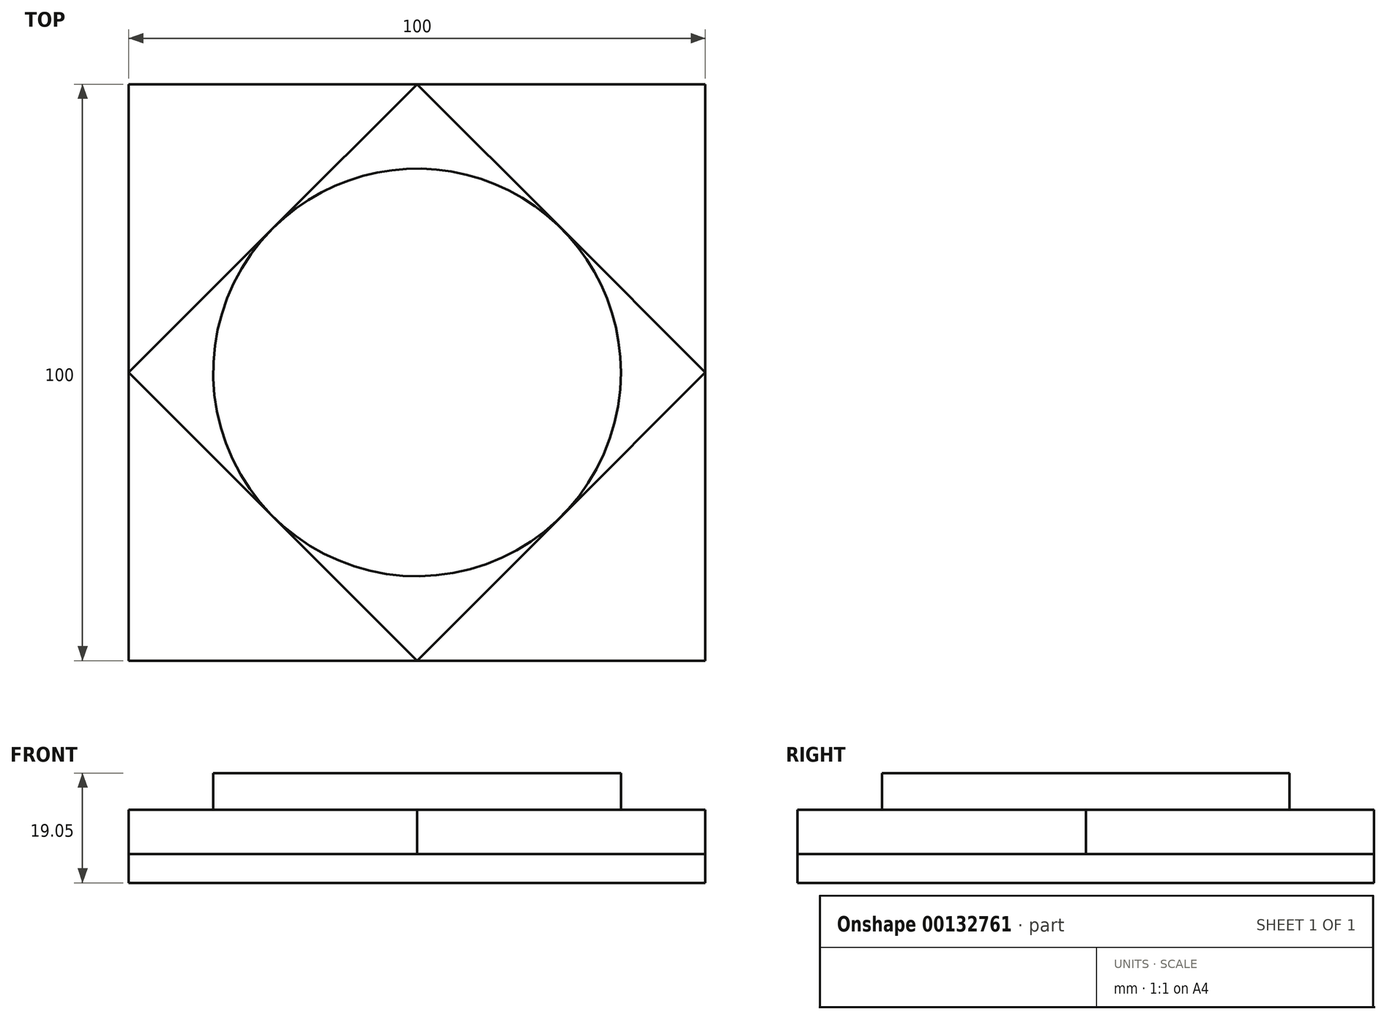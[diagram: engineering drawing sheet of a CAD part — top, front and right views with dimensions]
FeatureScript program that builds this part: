
annotation { "Feature Type Name" : "Feature", "Feature Type Description" : "" }
export const myFeature = defineFeature(function(context is Context, id is Id, definition is map)
    precondition{}
    {
        {
            var Q0;
            Q0=qCreatedBy(makeId("Top.planeOp"),FACE);
            var sketch = newSketch(context, id + "F0", { "sketchPlane" : qUnion([Q0])});
            skLineSegment(sketch, "E0.bottom", {"start": v(50, 50) * mm, "end": v(-50, 50) * mm});
            skLineSegment(sketch, "E0.top", {"start": v(50, -50) * mm, "end": v(-50, -50) * mm});
            skLineSegment(sketch, "E0.left", {"start": v(50, 50) * mm, "end": v(50, -50) * mm});
            skLineSegment(sketch, "E0.right", {"start": v(-50, 50) * mm, "end": v(-50, -50) * mm});
            skPoint(sketch, "E0.middle", {"position": v(0, 0) * mm});
            skCircle(sketch, "E1.cCircle", {"center": v(0, 0) * mm, "radius": 50 * mm, "construction": true});
            skLineSegment(sketch, "E1.0", {"start": v(50, 0) * mm, "end": v(0, -50) * mm});
            skLineSegment(sketch, "E1.1", {"start": v(0, -50) * mm, "end": v(-50, 0) * mm});
            skLineSegment(sketch, "E1.2", {"start": v(-50, 0) * mm, "end": v(0, 50) * mm});
            skLineSegment(sketch, "E1.3", {"start": v(0, 50) * mm, "end": v(50, 0) * mm});
            skCircle(sketch, "E2", {"center": v(0, 0) * mm, "radius": 35.36 * mm});
            skSolve(sketch);
        }
        {
            var Q0;
            {var subQ0=sQuery(id+"F0.wireOp",EDGE,"E0.left");var subQ1=sQuery(id+"F0.wireOp",EDGE,"E0.bottom");var subQ2=makeQuery(id+"F0.imprint","INTERSECT",VERTEX,{"derivedFrom":[subQ1,subQ0]});Q0=makeQuery(id+"F0.imprint","IMPRINT",FACE,{"disambiguationData":[TD([[makeQuery(id+"F0.imprint","IMPRINT",EDGE,{"disambiguationData":[TD([[subQ2,-1.0]])],"derivedFrom":subQ1}),1.0]])]});}
            var Q1;
            {var subQ0=sQuery(id+"F0.wireOp",EDGE,"E0.right");var subQ1=sQuery(id+"F0.wireOp",EDGE,"E0.bottom");var subQ2=makeQuery(id+"F0.imprint","INTERSECT",VERTEX,{"derivedFrom":[subQ1,subQ0]});Q1=makeQuery(id+"F0.imprint","IMPRINT",FACE,{"disambiguationData":[TD([[makeQuery(id+"F0.imprint","IMPRINT",EDGE,{"disambiguationData":[TD([[subQ2,1.0]])],"derivedFrom":subQ1}),1.0]])]});}
            var Q2;
            {var subQ0=sQuery(id+"F0.wireOp",EDGE,"E0.left");var subQ1=sQuery(id+"F0.wireOp",EDGE,"E0.top");var subQ2=makeQuery(id+"F0.imprint","INTERSECT",VERTEX,{"derivedFrom":[subQ1,subQ0]});Q2=makeQuery(id+"F0.imprint","IMPRINT",FACE,{"disambiguationData":[TD([[makeQuery(id+"F0.imprint","IMPRINT",EDGE,{"disambiguationData":[TD([[subQ2,-1.0]])],"derivedFrom":subQ1}),-1.0]])]});}
            var Q3;
            {var subQ0=sQuery(id+"F0.wireOp",EDGE,"E2");var subQ1=makeQuery(id+"F0.imprint","INTERSECT",VERTEX,{"derivedFrom":[sQuery(id+"F0.wireOp",EDGE,"E1.2"),subQ0]});Q3=makeQuery(id+"F0.imprint","IMPRINT",FACE,{"disambiguationData":[TD([[makeQuery(id+"F0.imprint","IMPRINT",EDGE,{"disambiguationData":[TD([[subQ1,1.0]])],"derivedFrom":subQ0}),1.0]])]});}
            var Q4;
            {var subQ1=sQuery(id+"F0.wireOp",EDGE,"E1.2");var subQ3=sQuery(id+"F0.wireOp",EDGE,"E2");var subQ4=makeQuery(id+"F0.imprint","INTERSECT",VERTEX,{"derivedFrom":[subQ1,subQ3]});Q4=makeQuery(id+"F0.imprint","IMPRINT",FACE,{"disambiguationData":[TD([[makeQuery(id+"F0.imprint","IMPRINT",EDGE,{"disambiguationData":[TD([[subQ4,1.0]])],"derivedFrom":subQ3}),-1.0]])]});}
            var Q5;
            {var subQ1=sQuery(id+"F0.wireOp",EDGE,"E1.1");var subQ3=sQuery(id+"F0.wireOp",EDGE,"E2");var subQ4=makeQuery(id+"F0.imprint","INTERSECT",VERTEX,{"derivedFrom":[subQ1,subQ3]});Q5=makeQuery(id+"F0.imprint","IMPRINT",FACE,{"disambiguationData":[TD([[makeQuery(id+"F0.imprint","IMPRINT",EDGE,{"disambiguationData":[TD([[subQ4,1.0]])],"derivedFrom":subQ3}),-1.0]])]});}
            var Q6;
            {var subQ0=sQuery(id+"F0.wireOp",EDGE,"E0.right");var subQ1=sQuery(id+"F0.wireOp",EDGE,"E0.top");var subQ2=makeQuery(id+"F0.imprint","INTERSECT",VERTEX,{"derivedFrom":[subQ1,subQ0]});Q6=makeQuery(id+"F0.imprint","IMPRINT",FACE,{"disambiguationData":[TD([[makeQuery(id+"F0.imprint","IMPRINT",EDGE,{"disambiguationData":[TD([[subQ2,1.0]])],"derivedFrom":subQ1}),-1.0]])]});}
            var Q7;
            {var subQ1=sQuery(id+"F0.wireOp",EDGE,"E1.0");var subQ3=sQuery(id+"F0.wireOp",EDGE,"E2");var subQ4=makeQuery(id+"F0.imprint","INTERSECT",VERTEX,{"derivedFrom":[subQ1,subQ3]});Q7=makeQuery(id+"F0.imprint","IMPRINT",FACE,{"disambiguationData":[TD([[makeQuery(id+"F0.imprint","IMPRINT",EDGE,{"disambiguationData":[TD([[subQ4,-1.0]])],"derivedFrom":subQ3}),-1.0]])]});}
            var Q8;
            {var subQ1=sQuery(id+"F0.wireOp",EDGE,"E1.0");var subQ3=sQuery(id+"F0.wireOp",EDGE,"E2");var subQ4=makeQuery(id+"F0.imprint","INTERSECT",VERTEX,{"derivedFrom":[subQ1,subQ3]});Q8=makeQuery(id+"F0.imprint","IMPRINT",FACE,{"disambiguationData":[TD([[makeQuery(id+"F0.imprint","IMPRINT",EDGE,{"disambiguationData":[TD([[subQ4,1.0]])],"derivedFrom":subQ3}),-1.0]])]});}
            extrude(context, id + "F1", {"entities" : qUnion([Q0, Q1, Q2, Q3, Q4, Q5, Q6, Q7, Q8]), "offsetDistance" : 25 * mm, "depth" : 5 * mm});
        }
        {
            var Q0;
            {var subQ1=sQuery(id+"F0.wireOp",EDGE,"E1.1");var subQ3=sQuery(id+"F0.wireOp",EDGE,"E2");var subQ4=makeQuery(id+"F0.imprint","INTERSECT",VERTEX,{"derivedFrom":[subQ1,subQ3]});Q0=makeQuery(id+"F0.imprint","IMPRINT",FACE,{"disambiguationData":[TD([[makeQuery(id+"F0.imprint","IMPRINT",EDGE,{"disambiguationData":[TD([[subQ4,1.0]])],"derivedFrom":subQ3}),-1.0]])]});}
            var Q1;
            {var subQ1=sQuery(id+"F0.wireOp",EDGE,"E1.0");var subQ3=sQuery(id+"F0.wireOp",EDGE,"E2");var subQ4=makeQuery(id+"F0.imprint","INTERSECT",VERTEX,{"derivedFrom":[subQ1,subQ3]});Q1=makeQuery(id+"F0.imprint","IMPRINT",FACE,{"disambiguationData":[TD([[makeQuery(id+"F0.imprint","IMPRINT",EDGE,{"disambiguationData":[TD([[subQ4,-1.0]])],"derivedFrom":subQ3}),-1.0]])]});}
            var Q2;
            {var subQ1=sQuery(id+"F0.wireOp",EDGE,"E1.0");var subQ3=sQuery(id+"F0.wireOp",EDGE,"E2");var subQ4=makeQuery(id+"F0.imprint","INTERSECT",VERTEX,{"derivedFrom":[subQ1,subQ3]});Q2=makeQuery(id+"F0.imprint","IMPRINT",FACE,{"disambiguationData":[TD([[makeQuery(id+"F0.imprint","IMPRINT",EDGE,{"disambiguationData":[TD([[subQ4,1.0]])],"derivedFrom":subQ3}),-1.0]])]});}
            var Q3;
            {var subQ0=sQuery(id+"F0.wireOp",EDGE,"E2");var subQ1=makeQuery(id+"F0.imprint","INTERSECT",VERTEX,{"derivedFrom":[sQuery(id+"F0.wireOp",EDGE,"E1.2"),subQ0]});Q3=makeQuery(id+"F0.imprint","IMPRINT",FACE,{"disambiguationData":[TD([[makeQuery(id+"F0.imprint","IMPRINT",EDGE,{"disambiguationData":[TD([[subQ1,1.0]])],"derivedFrom":subQ0}),1.0]])]});}
            var Q4;
            {var subQ1=sQuery(id+"F0.wireOp",EDGE,"E1.2");var subQ3=sQuery(id+"F0.wireOp",EDGE,"E2");var subQ4=makeQuery(id+"F0.imprint","INTERSECT",VERTEX,{"derivedFrom":[subQ1,subQ3]});Q4=makeQuery(id+"F0.imprint","IMPRINT",FACE,{"disambiguationData":[TD([[makeQuery(id+"F0.imprint","IMPRINT",EDGE,{"disambiguationData":[TD([[subQ4,1.0]])],"derivedFrom":subQ3}),-1.0]])]});}
            extrude(context, id + "F2", {"entities" : qUnion([Q0, Q1, Q2, Q3, Q4]), "operationType" : NewBodyOperationType.ADD, "depth" : 12.7 * mm});
        }
        {
            var Q0;
            {var subQ0=sQuery(id+"F0.wireOp",EDGE,"E2");var subQ1=makeQuery(id+"F0.imprint","INTERSECT",VERTEX,{"derivedFrom":[sQuery(id+"F0.wireOp",EDGE,"E1.2"),subQ0]});Q0=makeQuery(id+"F0.imprint","IMPRINT",FACE,{"disambiguationData":[TD([[makeQuery(id+"F0.imprint","IMPRINT",EDGE,{"disambiguationData":[TD([[subQ1,1.0]])],"derivedFrom":subQ0}),1.0]])]});}
            extrude(context, id + "F3", {"entities" : qUnion([Q0]), "operationType" : NewBodyOperationType.ADD, "depth" : 19.05 * mm});
        }
    });
